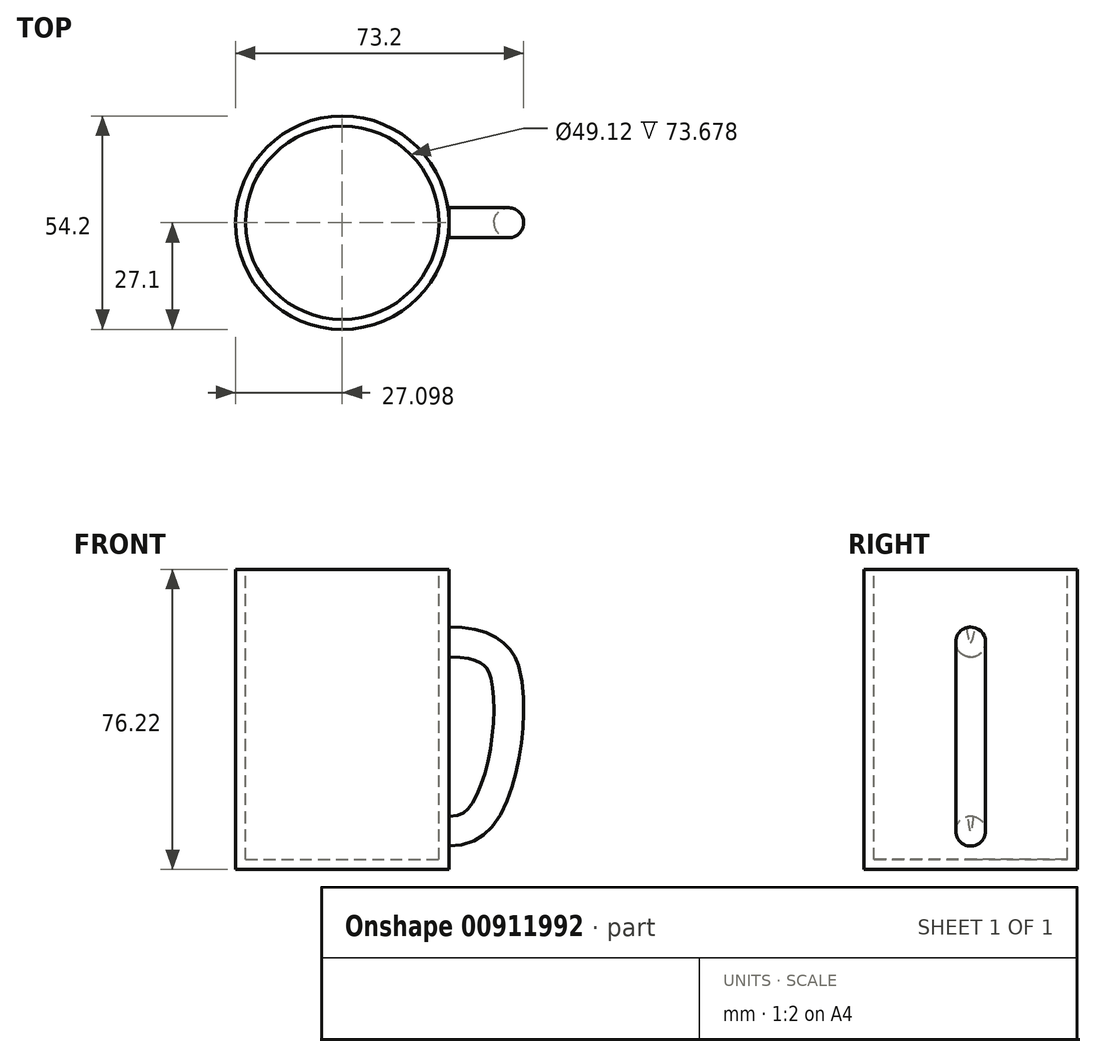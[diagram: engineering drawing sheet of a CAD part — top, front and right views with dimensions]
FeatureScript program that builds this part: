
annotation { "Feature Type Name" : "Feature", "Feature Type Description" : "" }
export const myFeature = defineFeature(function(context is Context, id is Id, definition is map)
    precondition{}
    {
        {
            var Q0;
            Q0=qCreatedBy(makeId("Front.planeOp"),FACE);
            var sketch = newSketch(context, id + "F0", { "sketchPlane" : qUnion([Q0])});
            skLineSegment(sketch, "E0.bottom", {"start": v(35.16, 35.17) * mm, "end": v(8.06, 35.17) * mm});
            skLineSegment(sketch, "E0.top", {"start": v(35.16, -41.05) * mm, "end": v(8.06, -41.05) * mm});
            skLineSegment(sketch, "E0.left", {"start": v(35.16, 35.17) * mm, "end": v(35.16, -41.05) * mm});
            skLineSegment(sketch, "E0.right", {"start": v(8.06, 35.17) * mm, "end": v(8.06, -41.05) * mm});
            skFitSpline(sketch, "E1", {"points": [v(31.2, 24.13) * mm, v(35.16, 25.66) * mm], "startDerivative": vector(0, 1.53) * mm, "endDerivative": vector(0, 1.53) * mm});
            skFitSpline(sketch, "E2", {"points": [v(35.16, 16.67) * mm, v(45.38, 14.5) * mm, v(49.2, 9.39) * mm, v(49.9, -7.06) * mm, v(45.02, -24.93) * mm, v(35.16, -31.24) * mm], "startDerivative": vector(76.07, 0.45) * mm, "endDerivative": vector(-81.2, -0.16) * mm});
            skSolve(sketch);
        }
        {
            var Q0;
            Q0=makeQuery(id+"F0.imprint","IMPRINT",FACE,{"disambiguationData":[TD([[makeQuery(id+"F0.imprint","IMPRINT",EDGE,{"derivedFrom":sQuery(id+"F0.wireOp",EDGE,"E0.bottom")}),1.0]])]});
            var Q1;
            Q1=sQuery(id+"F0.wireOp",EDGE,"E0.right");
            revolve(context, id + "F1", {"surfaceOperationType" : NewSurfaceOperationType.NEW, "entities" : qUnion([Q0]), "axis" : qUnion([Q1]), "revolveType" : RevolveType.FULL});
        }
        {
            var Q0;
            Q0=makeQuery(id+"F1.opRevolve","SWEPT_FACE",FACE,{"disambiguationData":[OSD([sQuery(id+"F0.wireOp",EDGE,"E0.bottom")])]});
            shell(context, id + "F2", {"entities" : qUnion([Q0]), "thickness" : 2.54 * mm});
        }
        {
            var Q0;
            Q0=sQuery(id+"F0.wireOp",EDGE,"E2");
            var Q1;
            Q1=sQuery(id+"F0.wireOp",VERTEX,"E2.end");
            cPlane(context, id + "F3", {"entities" : qUnion([Q0, Q1]), "cplaneType" : CPlaneType.CURVE_POINT, "offset" : 25.4 * mm, "width" : 152.4 * mm, "height" : 152.4 * mm});
        }
        {
            var Q0;
            Q0=qCreatedBy(id+"F3.planeOp",FACE);
            var sketch = newSketch(context, id + "F4", { "sketchPlane" : qUnion([Q0])});
            skCircle(sketch, "E3", {"center": v(0, -31.37) * mm, "radius": 3.8 * mm});
            skSolve(sketch);
        }
        {
            var Q0;
            Q0=makeQuery(id+"F4.imprint","IMPRINT",FACE,{"disambiguationData":[TD([[makeQuery(id+"F4.imprint","IMPRINT",EDGE,{"derivedFrom":sQuery(id+"F4.wireOp",EDGE,"E3")}),1.0]])]});
            var Q1;
            Q1=sQuery(id+"F0.wireOp",EDGE,"E2");
            sweep(context, id + "F5", {"operationType" : NewBodyOperationType.ADD, "profiles" : qUnion([Q0]), "path" : qUnion([Q1])});
        }
    });
